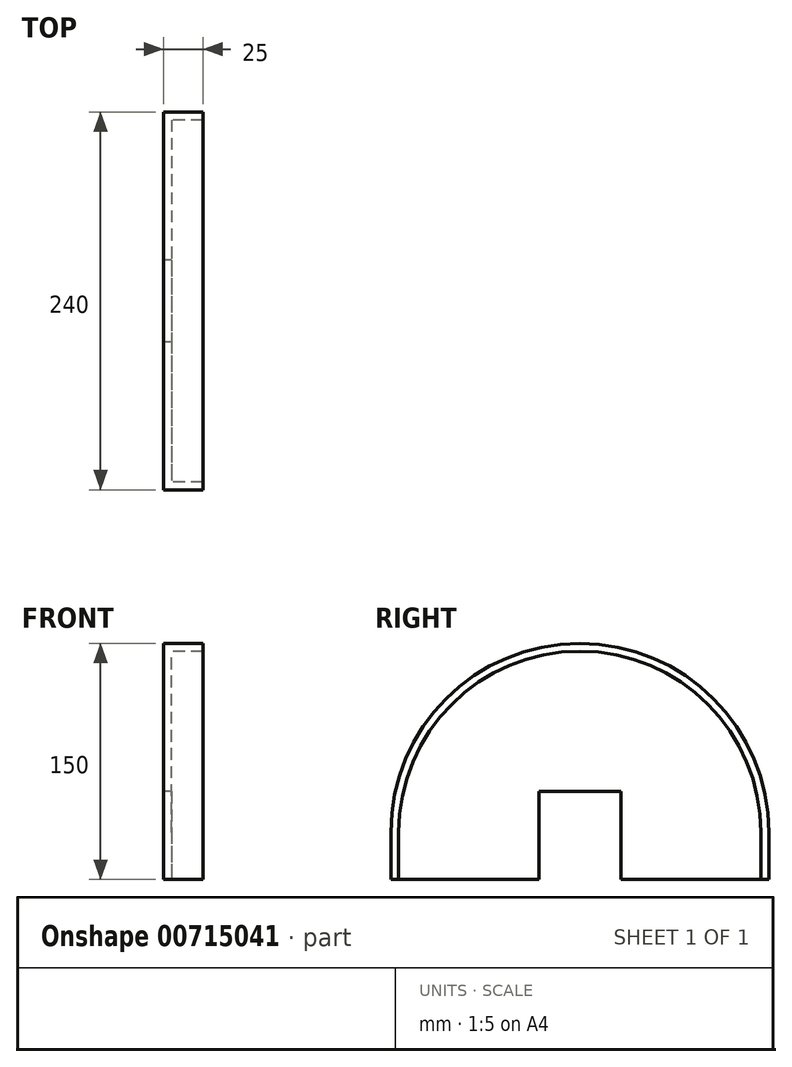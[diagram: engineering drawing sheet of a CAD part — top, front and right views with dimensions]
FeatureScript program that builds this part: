
annotation { "Feature Type Name" : "Feature", "Feature Type Description" : "" }
export const myFeature = defineFeature(function(context is Context, id is Id, definition is map)
    precondition{}
    {
        {
            var Q0;
            Q0=qCreatedBy(makeId("Right.planeOp"),FACE);
            var sketch = newSketch(context, id + "F0", { "sketchPlane" : qUnion([Q0])});
            skArc(sketch, "E0", {"start": v(115, 0) * mm, "mid": v(0, 115) * mm, "end": v(-115, 0) * mm});
            skPoint(sketch, "E1", {"position": v(115, 0) * mm});
            skPoint(sketch, "E2", {"position": v(120, 0) * mm});
            skLineSegment(sketch, "E3.top", {"start": v(115, -30) * mm, "end": v(116.19, -30) * mm});
            skLineSegment(sketch, "E3.left", {"start": v(115, 0) * mm, "end": v(115, -30) * mm});
            skLineSegment(sketch, "E3.right", {"start": v(120, 0) * mm, "end": v(120, -30) * mm});
            skPoint(sketch, "E4", {"position": v(-120, 0) * mm});
            skPoint(sketch, "E5", {"position": v(-115, 0) * mm});
            skPoint(sketch, "E6", {"position": v(116.19, -30) * mm});
            skArc(sketch, "E7", {"start": v(120, 0) * mm, "mid": v(0, 120) * mm, "end": v(-120, 0) * mm});
            skLineSegment(sketch, "E8", {"start": v(116.19, -30) * mm, "end": v(120, -30) * mm});
            skLineSegment(sketch, "E9", {"start": v(115, -30) * mm, "end": v(26, -30) * mm});
            skLineSegment(sketch, "E10", {"start": v(-115, 0) * mm, "end": v(-115, -30) * mm});
            skLineSegment(sketch, "E11", {"start": v(-120, 0) * mm, "end": v(-120, -30) * mm});
            skLineSegment(sketch, "E12", {"start": v(-115, -30) * mm, "end": v(-120, -30) * mm});
            skPoint(sketch, "E13", {"position": v(0, -30) * mm});
            skPoint(sketch, "E14", {"position": v(26, -30) * mm});
            skPoint(sketch, "E15", {"position": v(26, 26) * mm});
            skPoint(sketch, "E16", {"position": v(0, 26) * mm});
            skLineSegment(sketch, "E17", {"start": v(0, 26) * mm, "end": v(26, 26) * mm});
            skLineSegment(sketch, "E18", {"start": v(26, 26) * mm, "end": v(26, -30) * mm});
            skLineSegment(sketch, "E19.MirrorCS", {"start": v(0, 26) * mm, "end": v(-26, 26) * mm});
            skLineSegment(sketch, "E20.MirrorCS", {"start": v(-26, 26) * mm, "end": v(-26, -30) * mm});
            skLineSegment(sketch, "E21", {"start": v(-26, -30) * mm, "end": v(-115, -30) * mm});
            skSolve(sketch);
        }
        {
            var Q0;
            Q0=makeQuery(id+"F0.imprint","IMPRINT",FACE,{"disambiguationData":[TD([[makeQuery(id+"F0.imprint","IMPRINT",EDGE,{"derivedFrom":sQuery(id+"F0.wireOp",EDGE,"E0")}),1.0]])]});
            extrude(context, id + "F1", {"entities" : qUnion([Q0]), "depth" : 5 * mm, "offsetDistance" : 25 * mm});
        }
        {
            var Q0;
            Q0=makeQuery(id+"F0.imprint","IMPRINT",FACE,{"disambiguationData":[TD([[makeQuery(id+"F0.imprint","IMPRINT",EDGE,{"derivedFrom":sQuery(id+"F0.wireOp",EDGE,"E0")}),-1.0]])]});
            extrude(context, id + "F2", {"entities" : qUnion([Q0]), "operationType" : NewBodyOperationType.ADD, "depth" : 25 * mm, "offsetDistance" : 25 * mm});
        }
    });
